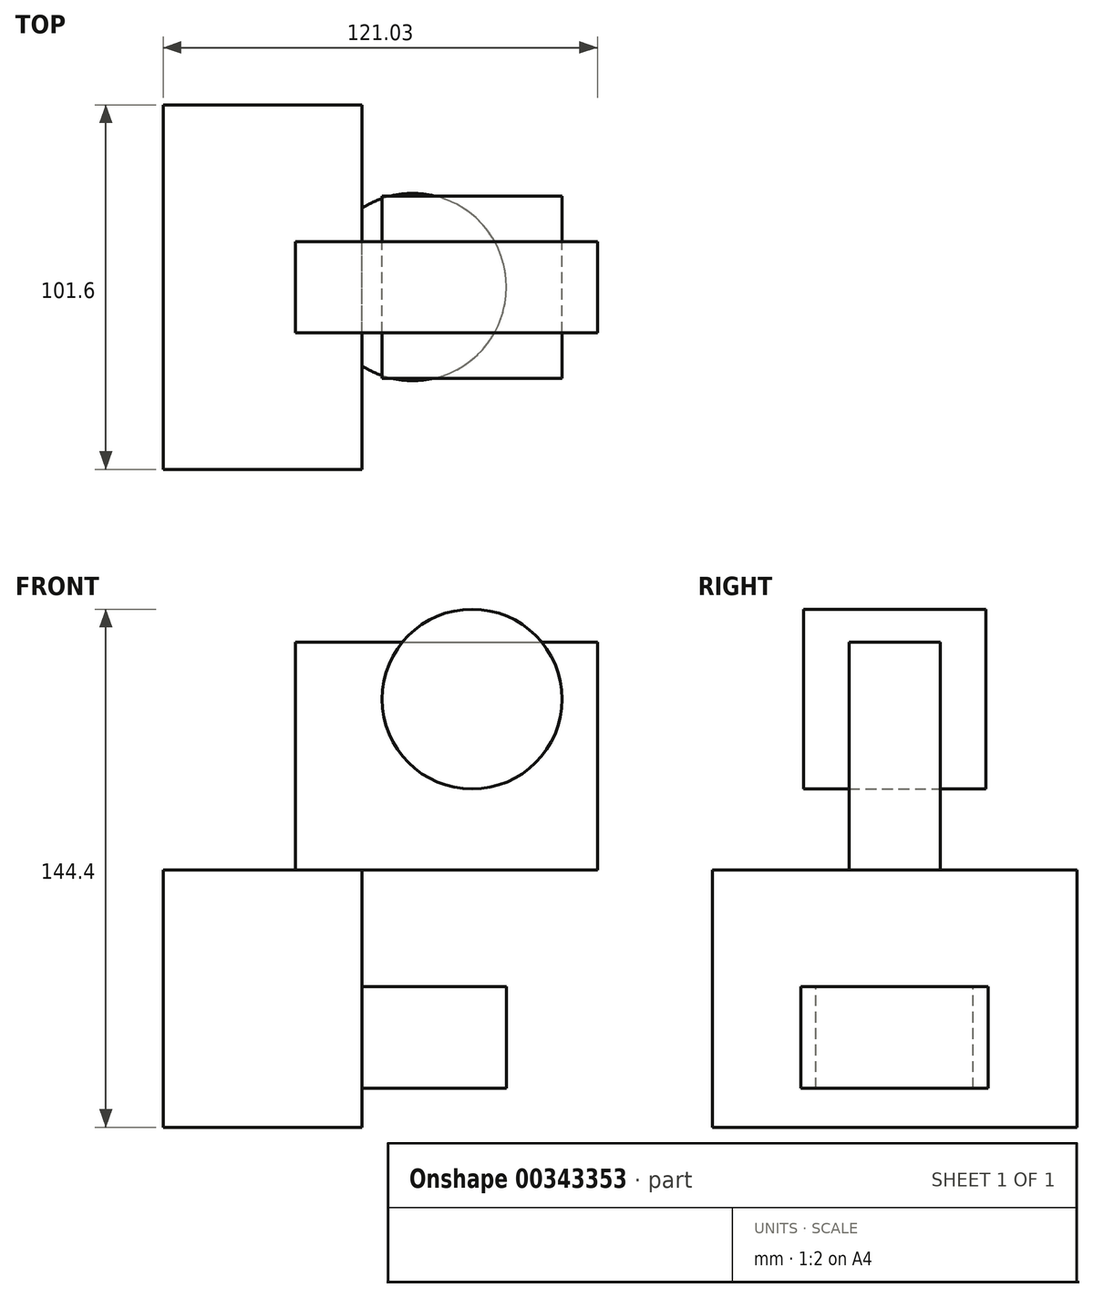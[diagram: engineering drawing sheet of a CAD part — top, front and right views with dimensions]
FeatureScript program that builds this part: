
annotation { "Feature Type Name" : "Feature", "Feature Type Description" : "" }
export const myFeature = defineFeature(function(context is Context, id is Id, definition is map)
    precondition{}
    {
        {
            var Q0;
            Q0=qCreatedBy(makeId("Front.planeOp"),FACE);
            var sketch = newSketch(context, id + "F0", { "sketchPlane" : qUnion([Q0])});
            skLineSegment(sketch, "E0.bottom", {"start": v(0, 0) * mm, "end": v(-55.39, 0) * mm});
            skLineSegment(sketch, "E0.top", {"start": v(0, -71.7) * mm, "end": v(-55.39, -71.7) * mm});
            skLineSegment(sketch, "E0.left", {"start": v(0, 0) * mm, "end": v(0, -71.7) * mm});
            skLineSegment(sketch, "E0.right", {"start": v(-55.39, 0) * mm, "end": v(-55.39, -71.7) * mm});
            skSolve(sketch);
        }
        {
            var Q0;
            Q0=makeQuery(id+"F0.imprint","IMPRINT",FACE,{"disambiguationData":[TD([[makeQuery(id+"F0.imprint","IMPRINT",EDGE,{"derivedFrom":sQuery(id+"F0.wireOp",EDGE,"E0.bottom")}),1.0]])]});
            extrude(context, id + "F1", {"entities" : qUnion([Q0]), "endBound" : BoundingType.SYMMETRIC, "depth" : 101.6 * mm});
        }
        {
            var Q0;
            Q0=qCreatedBy(makeId("Front.planeOp"),FACE);
            var sketch = newSketch(context, id + "F2", { "sketchPlane" : qUnion([Q0])});
            skCircle(sketch, "E1", {"center": v(30.72, 47.64) * mm, "radius": 25.06 * mm});
            skSolve(sketch);
        }
        {
            var Q0;
            Q0=makeQuery(id+"F2.imprint","IMPRINT",FACE,{"disambiguationData":[TD([[makeQuery(id+"F2.imprint","IMPRINT",EDGE,{"derivedFrom":sQuery(id+"F2.wireOp",EDGE,"E1")}),1.0]])]});
            extrude(context, id + "F3", {"entities" : qUnion([Q0]), "endBound" : BoundingType.SYMMETRIC, "depth" : 50.8 * mm});
        }
        {
            var Q0;
            Q0=qCreatedBy(makeId("Front.planeOp"),FACE);
            var sketch = newSketch(context, id + "F4", { "sketchPlane" : qUnion([Q0])});
            skLineSegment(sketch, "E2.bottom", {"start": v(-18.58, 0) * mm, "end": v(65.64, 0) * mm});
            skLineSegment(sketch, "E2.top", {"start": v(-18.58, 63.56) * mm, "end": v(65.64, 63.56) * mm});
            skLineSegment(sketch, "E2.left", {"start": v(-18.58, 0) * mm, "end": v(-18.58, 63.56) * mm});
            skLineSegment(sketch, "E2.right", {"start": v(65.64, 0) * mm, "end": v(65.64, 63.56) * mm});
            skSolve(sketch);
        }
        {
            var Q0;
            Q0=makeQuery(id+"F4.imprint","IMPRINT",FACE,{"disambiguationData":[TD([[makeQuery(id+"F4.imprint","IMPRINT",EDGE,{"derivedFrom":sQuery(id+"F4.wireOp",EDGE,"E2.bottom")}),1.0]])]});
            extrude(context, id + "F5", {"entities" : qUnion([Q0]), "endBound" : BoundingType.SYMMETRIC, "depth" : 25.4 * mm});
        }
        {
            var Q0;
            Q0=qCreatedBy(makeId("Front.planeOp"),FACE);
            var sketch = newSketch(context, id + "F6", { "sketchPlane" : qUnion([Q0])});
            skLineSegment(sketch, "E3.bottom", {"start": v(-11.96, -32.56) * mm, "end": v(14.16, -32.56) * mm});
            skLineSegment(sketch, "E3.top", {"start": v(-11.96, -60.88) * mm, "end": v(14.16, -60.88) * mm});
            skLineSegment(sketch, "E3.left", {"start": v(-11.96, -32.56) * mm, "end": v(-11.96, -60.88) * mm});
            skLineSegment(sketch, "E3.right", {"start": v(14.16, -32.56) * mm, "end": v(14.16, -60.88) * mm});
            skSolve(sketch);
        }
        {
            var Q0;
            Q0=makeQuery(id+"F6.imprint","IMPRINT",FACE,{"disambiguationData":[TD([[makeQuery(id+"F6.imprint","IMPRINT",EDGE,{"derivedFrom":sQuery(id+"F6.wireOp",EDGE,"E3.bottom")}),-1.0]])]});
            var Q1;
            Q1=sQuery(id+"F6.wireOp",EDGE,"E3.right");
            revolve(context, id + "F7", {"operationType" : NewBodyOperationType.ADD, "entities" : qUnion([Q0]), "axis" : qUnion([Q1]), "revolveType" : RevolveType.FULL});
        }
    });
